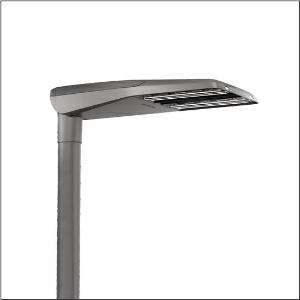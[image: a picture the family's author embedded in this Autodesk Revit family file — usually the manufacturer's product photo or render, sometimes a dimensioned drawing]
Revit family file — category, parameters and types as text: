
# Revit family: streetlight_sl_11_iq_midi___st1_0st0_5_5xc3j51g08me_56cc
name_source: partatom
category: Lighting Fixtures
units: mm (PartAtom-declared; Revit-internal decimal feet)

## family parameters
Cut with Voids When Loaded = No
Host = Face
Light Source = No
Part Type = Normal
Room Calculation Point = No
Round Connector Dimension = Use Diameter
Shared = No

## types (1)
- --- (1 x LED, 9460 lm, 63 W, 3000K)
    Apparent Load = 63 VA
    CIE Flux Codes = 35 68 96 100 100
    Color Rendering = 70
    Color Temperature = 3000K
    Default Elevation = 1800 mm
    Description = Streetlight SL 11 iQ midi, mast luminaire, primary light control with 3 zone facetted reflector, of plastic, silver coated, highly specular, primary optical cover: cover, of PMMA, transparent, light distribution: ST1.0ST0.5, light emission: direct distribution, primary light characteristic: asymmetric, installation type: post-top, side-entry, LED, High Power LED, rated luminous flux: 9.460lm, luminous efficacy: 150lm/W, light colour: 730, colour temperature: 3000K, control: Street-Remote, Auto-Match, Temp-Guard, Lumen-Switch, Night-Set, Smart-Wire, Light-Fading, Desk-Remote (wireless, voltage-free reading and setting of iQ features in the workshop via application-optimized NFC function/RFID function), optimised constant luminous flux control (CLO 2.0), presetting dimming linear, with cable H07RN-F 5x 1.5mm², mains connection: 230..240V, AC, 50/60Hz, connection cable pre-assembled, cable length: 12,5m, start of lifetime: 63W, end of service life: 67W, reduction: 30W, luminaire housing, of diecast aluminium, powder-coated, Siteco® metallic grey (DB 702S), please order mast flange separately, inclination adjustable without tools: 0°, 5°, 10°, 15° (post-top) | 0°, -5°, -10°, -15° (side-entry), sealing non-destructively replaceable, multi-level sealing system, length: 780mm, width: 376mm, height: 118mm, mast flange for spigot size: 42mm (side-entry): 5XC10008XM4, 60/48mm (side-entry/post-top): 5XC10108XM2, 76/60mm (side-entry/post-top): 5XC10108XM1, equipment: Power, protection rating (complete): IP66, insulation class (complete): insulation class II (safety insulation), certification: CE, ENEC, VDE, impact resistance: IK09, permissible operating ambient temperature for outdoor applications: -25..+50°C, standard-compliant lighting for roads and squares, Environmental Product Declaration (EPD) tested and certified by an independent institute, packaging unit: 1 piece

Light Distribution: ST1.0ST0.5
    Height = 118 mm
    Lamp = 1 x LED
    Lamp Light Flux = 9460 lm
    Lamp Power = 63 W
    Lamp count = 1
    Length = 780 mm
    Luminous efficacy = 150 lm/W
    Manufacturer = Siteco
    ModVariant = No
    Model = 5XC3J51G08ME
    Number of Poles = 1
    OnlyDefault = Yes
    Power Factor = 1
    Product Name = Streetlight SL 11 iQ midi | ST1.0ST0.5
    Product group = mast luminaire | pylon top
    ProductGroupID = 6100
    Protection Class = Protection class II
    Protection Degree = IP 66
    RLX_Detail_Level = 1
    RLX_Emergency_Light_Flux = 0 lm
    RLX_Emergency_Type = 0
    RLX_Emergency_Type_DB = No
    RlxData = <blob elided: 70525 chars, md5=aeae3244>
    Socket = socket
    Standby Power = 0 W
    System Light Flux = 9460 lm
    System Power = 63 W
    Type Comments = factory setting: luminous flux: 100 % | dim-lin: 254 | 553 mA
    Type Image = l_1005960.jpg
    URL = http://relux.com
    VarID = @adj_021799
    Voltage = 0 V
    Weight = 0.00 kg
    Width = 376 mm

## geometry (parser evidence)
native form markers: Blend x4, Sweep x9
no freeform markers — native parametric forms only
